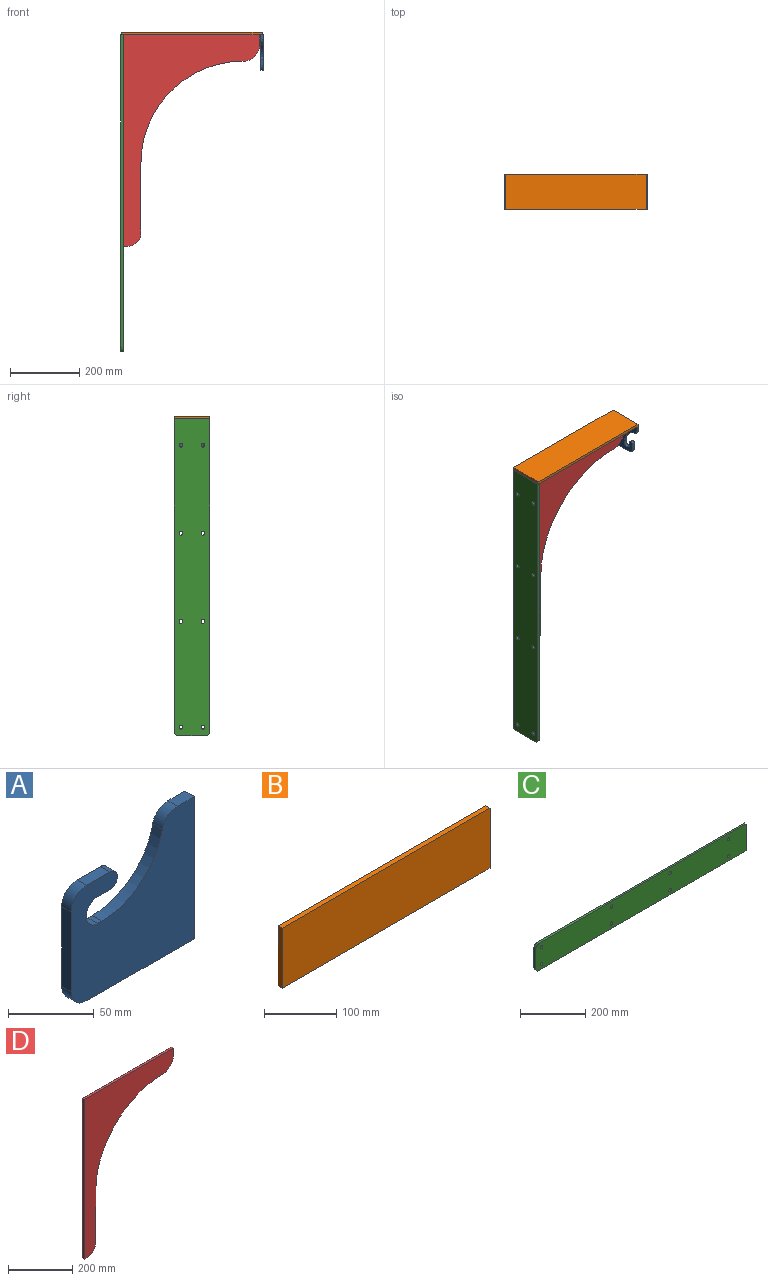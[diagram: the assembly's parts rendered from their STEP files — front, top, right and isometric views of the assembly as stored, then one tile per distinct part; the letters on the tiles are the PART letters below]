
ASSEMBLY  parts=4 mates=4
PART A: 17 faces, bbox 101.6x7.9x101.6 mm
  f0: plane 88.9x7.92mm, normal (0,0,-1), area 704.5mm2, adj f1,f8,f9,f15
  f1: plane 101.6x7.92mm, normal (1,0,0), area 805.2mm2, adj f0,f2,f8,f9
  f2: plane 13.98x7.92mm, normal (0,0,1), area 110.8mm2, adj f1,f8,f9,f16
  f3: plane 7.92x3.81mm, normal (0,0,1), area 30.2mm2, adj f8,f9,f11,f14
  f4: plane 7.92x1.27mm, normal (1,0,0), area 10.1mm2, adj f8,f9,f11,f12
  f5: plane 10.16x7.92mm, normal (0,0,-1), area 80.5mm2, adj f8,f9,f12,f13
  f6: plane 19.05x7.92mm, normal (0,0,1), area 151mm2, adj f8,f9,f10,f13
  f7: plane 57.15x7.92mm, normal (-1,0,0), area 452.9mm2, adj f8,f9,f10,f15
  f8: plane 101.6x101.6mm, normal (0,-1,0), area 7653.8mm2, adj f0,f1,f2,f3,f4,f5,f6,f7
  f9: plane 101.6x101.6mm, normal (0,1,0), area 7653.8mm2, adj f0,f1,f2,f3,f4,f5,f6,f7
  f10: cylinder r=12.7mm len=12.7mm, axis (0,1,0), area 158.1mm2, adj f6,f7,f8,f9
  f11: cylinder r=8.89mm len=8.89mm, axis (0,-1,0), area 110.7mm2, adj f3,f4,f8,f9
  f12: cylinder r=8.89mm len=8.89mm, axis (0,-1,0), area 110.7mm2, adj f4,f5,f8,f9
  f13: cylinder r=6.35mm len=12.7mm, axis (0,1,0), area 158.1mm2, adj f5,f6,f8,f9
  f14: cylinder r=50.8mm len=49.77mm, axis (0,-1,0), area 551.3mm2, adj f3,f8,f9,f16
  f15: cylinder r=12.7mm len=12.7mm, axis (0,1,0), area 158.1mm2, adj f0,f7,f8,f9
  f16: cylinder r=12.7mm len=12.44mm, axis (0,-1,0), area 137.8mm2, adj f2,f8,f9,f14
PART B: 6 faces, bbox 406.4x7.9x101.6 mm
  f0: plane 406.4x7.92mm, normal (0,0,-1), area 3220.6mm2, adj f1,f3,f4,f5
  f1: plane 101.6x7.92mm, normal (1,0,0), area 805.2mm2, adj f0,f2,f4,f5
  f2: plane 406.4x7.92mm, normal (0,0,1), area 3220.6mm2, adj f1,f3,f4,f5
  f3: plane 101.6x7.92mm, normal (-1,0,0), area 805.2mm2, adj f0,f2,f4,f5
  f4: plane 406.4x101.6mm, normal (0,-1,0), area 41290.2mm2, adj f0,f1,f2,f3
  f5: plane 406.4x101.6mm, normal (0,1,0), area 41290.2mm2, adj f0,f1,f2,f3
PART C: 16 faces, bbox 914.4x7.9x101.6 mm
  f0: plane 901.7x7.92mm, normal (0,0,-1), area 7145.8mm2, adj f1,f12,f13,f15
  f1: plane 101.6x7.92mm, normal (1,0,0), area 805.2mm2, adj f0,f2,f12,f13
  f2: plane 901.7x7.92mm, normal (0,0,1), area 7145.8mm2, adj f1,f12,f13,f14
  f3: cylinder r=5.52mm len=11.05mm, axis (0,1,0), area 275.1mm2, adj f12,f13
  f4: cylinder r=5.52mm len=11.05mm, axis (0,1,0), area 275.1mm2, adj f12,f13
  f5: cylinder r=5.52mm len=11.05mm, axis (0,1,0), area 275.1mm2, adj f12,f13
  f6: cylinder r=5.52mm len=11.05mm, axis (0,1,0), area 275.1mm2, adj f12,f13
  f7: cylinder r=5.52mm len=11.05mm, axis (0,1,0), area 275.1mm2, adj f12,f13
  f8: cylinder r=5.52mm len=11.05mm, axis (0,1,0), area 275.1mm2, adj f12,f13
  f9: cylinder r=5.52mm len=11.05mm, axis (0,1,0), area 275.1mm2, adj f12,f13
  f10: cylinder r=5.52mm len=11.05mm, axis (0,1,0), area 275.1mm2, adj f12,f13
  f11: plane 76.2x7.92mm, normal (-1,0,0), area 603.9mm2, adj f12,f13,f14,f15
  f12: plane 914.4x101.6mm, normal (0,-1,0), area 92066.8mm2, adj f0,f1,f2,f3,f4,f5,f6,f7
  f13: plane 914.4x101.6mm, normal (0,1,0), area 92066.8mm2, adj f0,f1,f2,f3,f4,f5,f6,f7
  f14: cylinder r=12.7mm len=12.7mm, axis (0,-1,0), area 158.1mm2, adj f2,f11,f12,f13
  f15: cylinder r=12.7mm len=12.7mm, axis (0,1,0), area 158.1mm2, adj f0,f11,f12,f13
PART D: 11 faces, bbox 393.7x7.9x609.6 mm
  f0: plane 609.6x7.92mm, normal (-1,0,0), area 4831mm2, adj f1,f5,f6,f7
  f1: plane 12.7x7.92mm, normal (0,0,-1), area 100.6mm2, adj f0,f6,f7,f9
  f2: plane 200.96x7.92mm, normal (1,0,0), area 1592.6mm2, adj f6,f7,f8,f9
  f3: plane 7.92x0.12mm, normal (0,0,-1), area 0.9mm2, adj f6,f7,f8,f10
  f4: plane 27.76x7.92mm, normal (1,0,0), area 220mm2, adj f5,f6,f7,f10
  f5: plane 393.7x7.92mm, normal (0,0,1), area 3120mm2, adj f0,f4,f6,f7
  f6: plane 609.6x393.7mm, normal (0,-1,0), area 74873.9mm2, adj f0,f1,f2,f3,f4,f5,f8,f9
  f7: plane 609.6x393.7mm, normal (0,1,0), area 74873.9mm2, adj f0,f1,f2,f3,f4,f5,f8,f9
  f8: cylinder r=294.34mm len=294.34mm, axis (0,-1,0), area 3664mm2, adj f2,f3,f6,f7
  f9: cylinder r=38.1mm len=38.1mm, axis (0,1,0), area 474.3mm2, adj f1,f2,f6,f7
  f10: cylinder r=48.44mm len=48.44mm, axis (0,-1,0), area 603mm2, adj f3,f4,f6,f7
PLACE A rot(axis=(0.58,-0.58,0.58),120deg) t=(240.78,233.15,637.64)mm
PLACE B rot(axis=(1,0,0),90deg) t=(244.75,233.15,645.57)mm
PLACE C rot(axis=(0.58,-0.58,0.58),120deg) t=(-163.23,233.15,637.64)mm
PLACE D t=(-155.3,186.31,28.04)mm
MATE planar B.f4 <-> D.f5  axis (0,0,-1) through (41.55,182.35,637.64)mm
MATE planar A.f1 <-> B.f4  axis (0,0,1) through (244.75,182.35,637.64)mm
MATE planar C.f12 <-> D.f0  axis (1,0,0) through (-155.3,182.35,180.89)mm
MATE planar D.f5 <-> C.f1  axis (0,0,1) through (-155.3,182.35,637.64)mm
